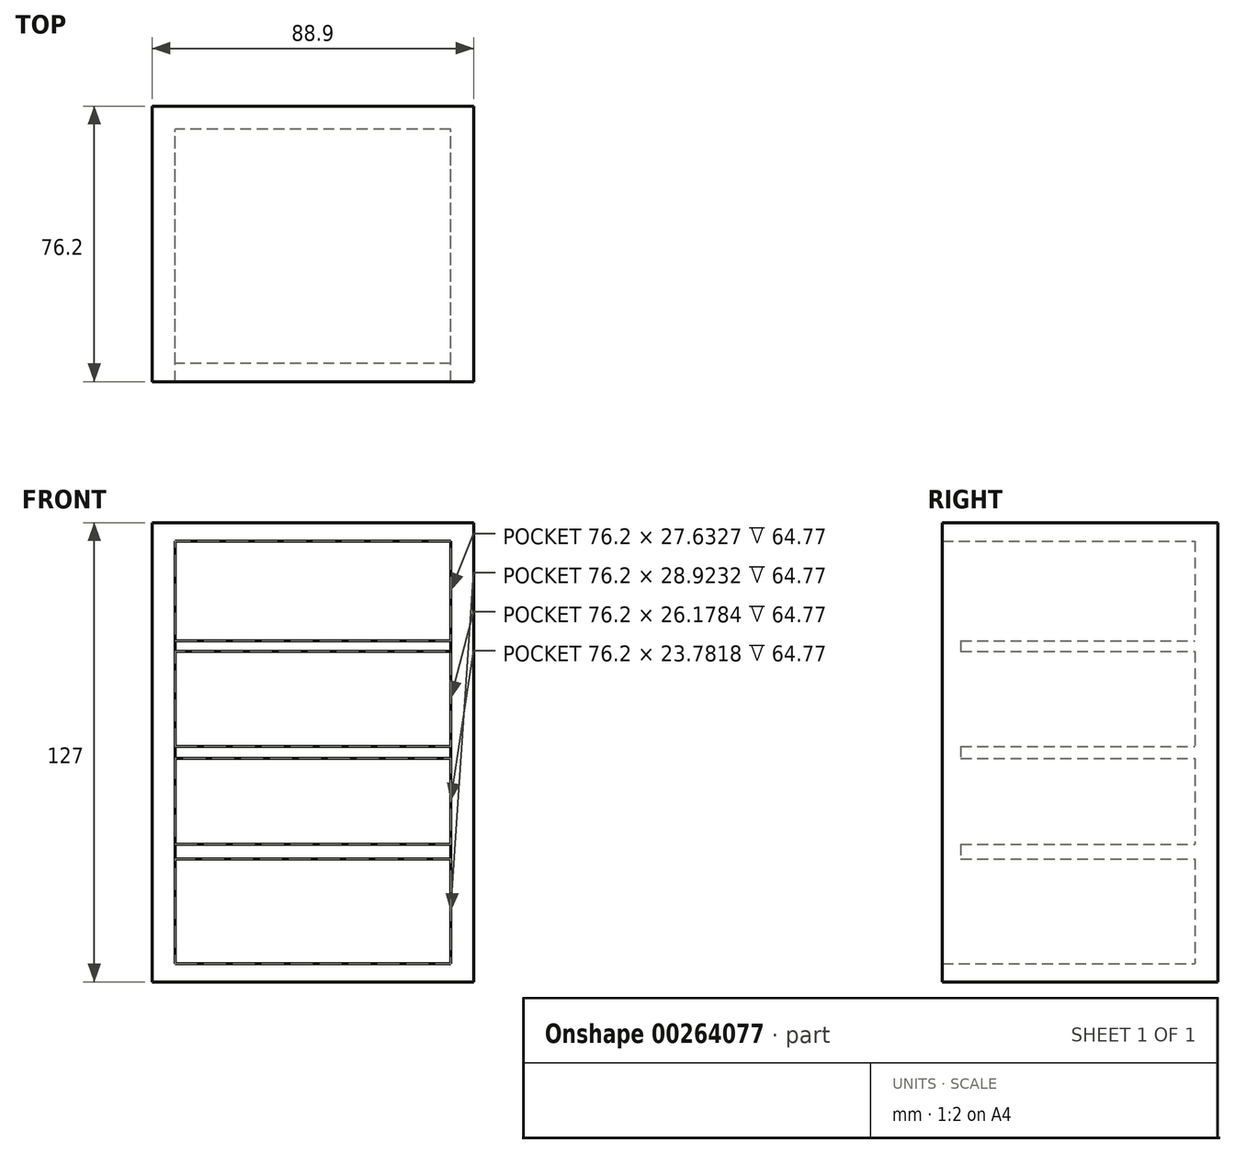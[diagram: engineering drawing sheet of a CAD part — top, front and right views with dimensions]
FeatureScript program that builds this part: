
annotation { "Feature Type Name" : "Feature", "Feature Type Description" : "" }
export const myFeature = defineFeature(function(context is Context, id is Id, definition is map)
    precondition{}
    {
        {
            var Q0;
            Q0=qCreatedBy(makeId("Front.planeOp"),FACE);
            var sketch = newSketch(context, id + "F0", { "sketchPlane" : qUnion([Q0])});
            skLineSegment(sketch, "E0.bottom", {"start": v(45.9, 63.5) * mm, "end": v(-43, 63.5) * mm});
            skLineSegment(sketch, "E0.top", {"start": v(45.9, -63.5) * mm, "end": v(-43, -63.5) * mm});
            skLineSegment(sketch, "E0.left", {"start": v(45.9, 63.5) * mm, "end": v(45.9, -63.5) * mm});
            skLineSegment(sketch, "E0.right", {"start": v(-43, 63.5) * mm, "end": v(-43, -63.5) * mm});
            skPoint(sketch, "E0.middle", {"position": v(1.44, 0) * mm});
            skLineSegment(sketch, "E1.bottom", {"start": v(39.54, 58.42) * mm, "end": v(-36.66, 58.42) * mm});
            skLineSegment(sketch, "E1.top", {"start": v(39.54, -58.42) * mm, "end": v(-36.66, -58.42) * mm});
            skLineSegment(sketch, "E1.left", {"start": v(39.54, 58.42) * mm, "end": v(39.54, -58.42) * mm});
            skLineSegment(sketch, "E1.right", {"start": v(-36.66, 58.42) * mm, "end": v(-36.66, -58.42) * mm});
            skLineSegment(sketch, "E2.bottom", {"start": v(39.54, 30.79) * mm, "end": v(-36.66, 30.79) * mm});
            skLineSegment(sketch, "E2.top", {"start": v(39.54, 27.84) * mm, "end": v(-36.66, 27.84) * mm});
            skLineSegment(sketch, "E2.left", {"start": v(39.54, 30.79) * mm, "end": v(39.54, 27.84) * mm});
            skLineSegment(sketch, "E2.right", {"start": v(-36.66, 30.79) * mm, "end": v(-36.66, 27.84) * mm});
            skPoint(sketch, "E2.middle", {"position": v(1.44, 29.31) * mm});
            skLineSegment(sketch, "E3.bottom", {"start": v(39.54, 1.66) * mm, "end": v(-36.66, 1.66) * mm});
            skLineSegment(sketch, "E3.top", {"start": v(39.54, -1.66) * mm, "end": v(-36.66, -1.66) * mm});
            skLineSegment(sketch, "E3.left", {"start": v(39.54, 1.66) * mm, "end": v(39.54, -1.66) * mm});
            skLineSegment(sketch, "E3.right", {"start": v(-36.66, 1.66) * mm, "end": v(-36.66, -1.66) * mm});
            skLineSegment(sketch, "E4.bottom", {"start": v(39.54, -25.44) * mm, "end": v(-36.66, -25.44) * mm});
            skLineSegment(sketch, "E4.top", {"start": v(39.54, -29.5) * mm, "end": v(-36.66, -29.5) * mm});
            skLineSegment(sketch, "E4.left", {"start": v(39.54, -25.44) * mm, "end": v(39.54, -29.5) * mm});
            skLineSegment(sketch, "E4.right", {"start": v(-36.66, -25.44) * mm, "end": v(-36.66, -29.5) * mm});
            skPoint(sketch, "E4.middle", {"position": v(1.44, -27.47) * mm});
            skSolve(sketch);
        }
        {
            var Q0;
            Q0=makeQuery(id+"F0.imprint","IMPRINT",FACE,{"disambiguationData":[TD([[makeQuery(id+"F0.imprint","IMPRINT",EDGE,{"derivedFrom":sQuery(id+"F0.wireOp",EDGE,"E0.bottom")}),1.0]])]});
            extrude(context, id + "F1", {"entities" : qUnion([Q0]), "depth" : 76.2 * mm});
        }
        {
            var Q0;
            Q0=makeQuery(id+"F0.imprint","IMPRINT",FACE,{"disambiguationData":[TD([[makeQuery(id+"F0.imprint","IMPRINT",EDGE,{"derivedFrom":sQuery(id+"F0.wireOp",EDGE,"E4.bottom")}),1.0]])]});
            var Q1;
            Q1=makeQuery(id+"F0.imprint","IMPRINT",FACE,{"disambiguationData":[TD([[makeQuery(id+"F0.imprint","IMPRINT",EDGE,{"derivedFrom":sQuery(id+"F0.wireOp",EDGE,"E3.bottom")}),1.0]])]});
            var Q2;
            Q2=makeQuery(id+"F0.imprint","IMPRINT",FACE,{"disambiguationData":[TD([[makeQuery(id+"F0.imprint","IMPRINT",EDGE,{"derivedFrom":sQuery(id+"F0.wireOp",EDGE,"E2.bottom")}),1.0]])]});
            extrude(context, id + "F2", {"entities" : qUnion([Q0, Q1, Q2]), "operationType" : NewBodyOperationType.ADD, "depth" : 71.12 * mm});
        }
        {
            var Q0;
            {var subQ0=sQuery(id+"F0.wireOp",EDGE,"E1.bottom");Q0=makeQuery(id+"F0.imprint","IMPRINT",FACE,{"disambiguationData":[TD([[makeQuery(id+"F0.imprint","IMPRINT",EDGE,{"derivedFrom":subQ0}),1.0]])]});}
            var Q1;
            {var subQ0=sQuery(id+"F0.wireOp",EDGE,"E2.top");Q1=makeQuery(id+"F0.imprint","IMPRINT",FACE,{"disambiguationData":[TD([[makeQuery(id+"F0.imprint","IMPRINT",EDGE,{"derivedFrom":subQ0}),1.0]])]});}
            var Q2;
            {var subQ0=sQuery(id+"F0.wireOp",EDGE,"E3.top");Q2=makeQuery(id+"F0.imprint","IMPRINT",FACE,{"disambiguationData":[TD([[makeQuery(id+"F0.imprint","IMPRINT",EDGE,{"derivedFrom":subQ0}),1.0]])]});}
            var Q3;
            {var subQ0=sQuery(id+"F0.wireOp",EDGE,"E1.top");Q3=makeQuery(id+"F0.imprint","IMPRINT",FACE,{"disambiguationData":[TD([[makeQuery(id+"F0.imprint","IMPRINT",EDGE,{"derivedFrom":subQ0}),-1.0]])]});}
            extrude(context, id + "F3", {"entities" : qUnion([Q0, Q1, Q2, Q3]), "operationType" : NewBodyOperationType.ADD, "depth" : 6.35 * mm});
        }
    });
